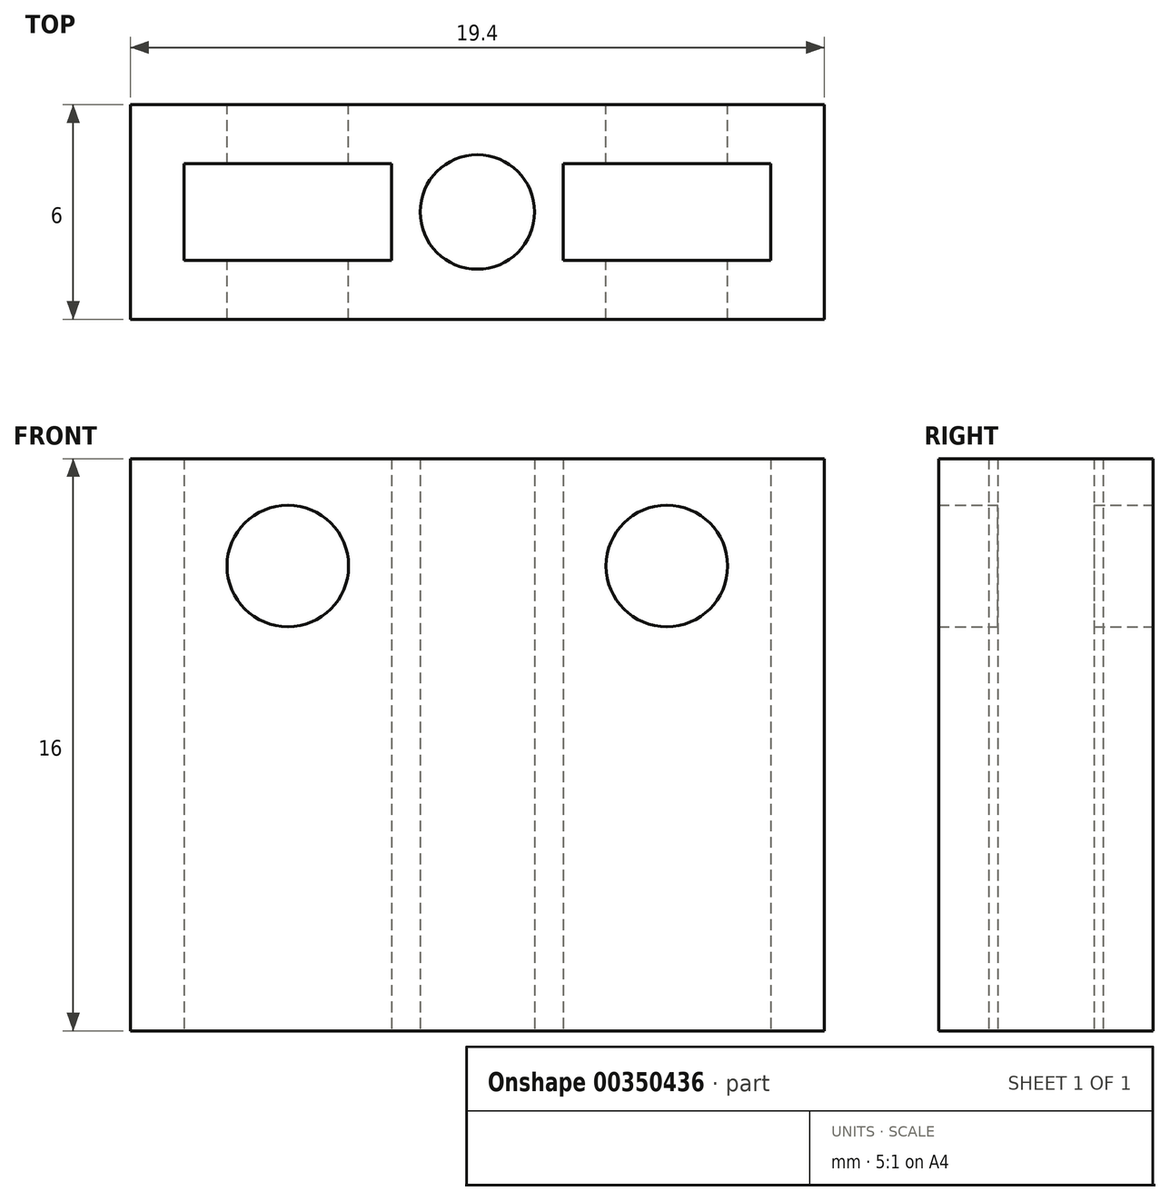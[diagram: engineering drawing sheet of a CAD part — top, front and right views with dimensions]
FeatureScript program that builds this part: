
annotation { "Feature Type Name" : "Feature", "Feature Type Description" : "" }
export const myFeature = defineFeature(function(context is Context, id is Id, definition is map)
    precondition{}
    {
        {
            var Q0;
            Q0=qCreatedBy(makeId("Top.planeOp"),FACE);
            var sketch = newSketch(context, id + "F0", { "sketchPlane" : qUnion([Q0])});
            skLineSegment(sketch, "E0", {"start": v(0, 1.6) * mm, "end": v(0, 3) * mm});
            skLineSegment(sketch, "E1", {"start": v(0, 3) * mm, "end": v(-9.7, 3) * mm});
            skLineSegment(sketch, "E2", {"start": v(-9.7, 3) * mm, "end": v(-9.7, 0) * mm});
            skLineSegment(sketch, "E3", {"start": v(-9.7, 0) * mm, "end": v(-9.7, -3) * mm});
            skLineSegment(sketch, "E4", {"start": v(-9.7, -3) * mm, "end": v(0, -3) * mm});
            skLineSegment(sketch, "E5", {"start": v(0, -3) * mm, "end": v(0, -1.6) * mm});
            skArc(sketch, "E6", {"start": v(0, 1.6) * mm, "mid": v(-1.6, 0) * mm, "end": v(0, -1.6) * mm});
            skLineSegment(sketch, "E7", {"start": v(-8.2, 0) * mm, "end": v(-8.2, 1.35) * mm});
            skLineSegment(sketch, "E8", {"start": v(-8.2, 1.35) * mm, "end": v(-2.4, 1.35) * mm});
            skLineSegment(sketch, "E9", {"start": v(-2.4, 1.35) * mm, "end": v(-2.4, -1.35) * mm});
            skLineSegment(sketch, "E10", {"start": v(-2.4, -1.35) * mm, "end": v(-8.2, -1.35) * mm});
            skLineSegment(sketch, "E11", {"start": v(-8.2, -1.35) * mm, "end": v(-8.2, 0) * mm});
            skSolve(sketch);
        }
        {
            var Q0;
            Q0 = qSketchRegion(id + "F0", true);
            extrude(context, id + "F1", {"entities" : qUnion([Q0]), "depth" : 16 * mm});
        }
        {
            var Q0;
            Q0=makeQuery(id+"F1.opExtrude","SWEPT_FACE",FACE,{"disambiguationData":[OSD([sQuery(id+"F0.wireOp",EDGE,"E1")])]});
            var sketch = newSketch(context, id + "F2", { "sketchPlane" : qUnion([Q0])});
            skCircle(sketch, "E12", {"center": v(5.3, 13) * mm, "radius": 1.7 * mm});
            skSolve(sketch);
        }
        {
            var Q0;
            Q0 = qSketchRegion(id + "F2", true);
            extrude(context, id + "F3", {"entities" : qUnion([Q0]), "operationType" : NewBodyOperationType.REMOVE, "oppositeDirection" : true, "depth" : 25 * mm});
        }
        {
            var Q0;
            Q0=makeQuery(id+"F1.opExtrude","SWEPT_BODY",BODY,{"disambiguationData":[OSD([sQuery(id+"F0.wireOp",EDGE,"E0"),sQuery(id+"F0.wireOp",EDGE,"E1"),sQuery(id+"F0.wireOp",EDGE,"E2"),sQuery(id+"F0.wireOp",EDGE,"E3"),sQuery(id+"F0.wireOp",EDGE,"E4"),sQuery(id+"F0.wireOp",EDGE,"E5"),sQuery(id+"F0.wireOp",EDGE,"E6"),sQuery(id+"F0.wireOp",EDGE,"E7"),sQuery(id+"F0.wireOp",EDGE,"E8"),sQuery(id+"F0.wireOp",EDGE,"E9"),sQuery(id+"F0.wireOp",EDGE,"E10"),sQuery(id+"F0.wireOp",EDGE,"E11")])]});
            var Q1;
            Q1=qCreatedBy(makeId("Right.planeOp"),FACE);
            mirror(context, id + "F4", {"operationType" : NewBodyOperationType.ADD, "entities" : qUnion([Q0]), "mirrorPlane" : qUnion([Q1])});
        }
    });
